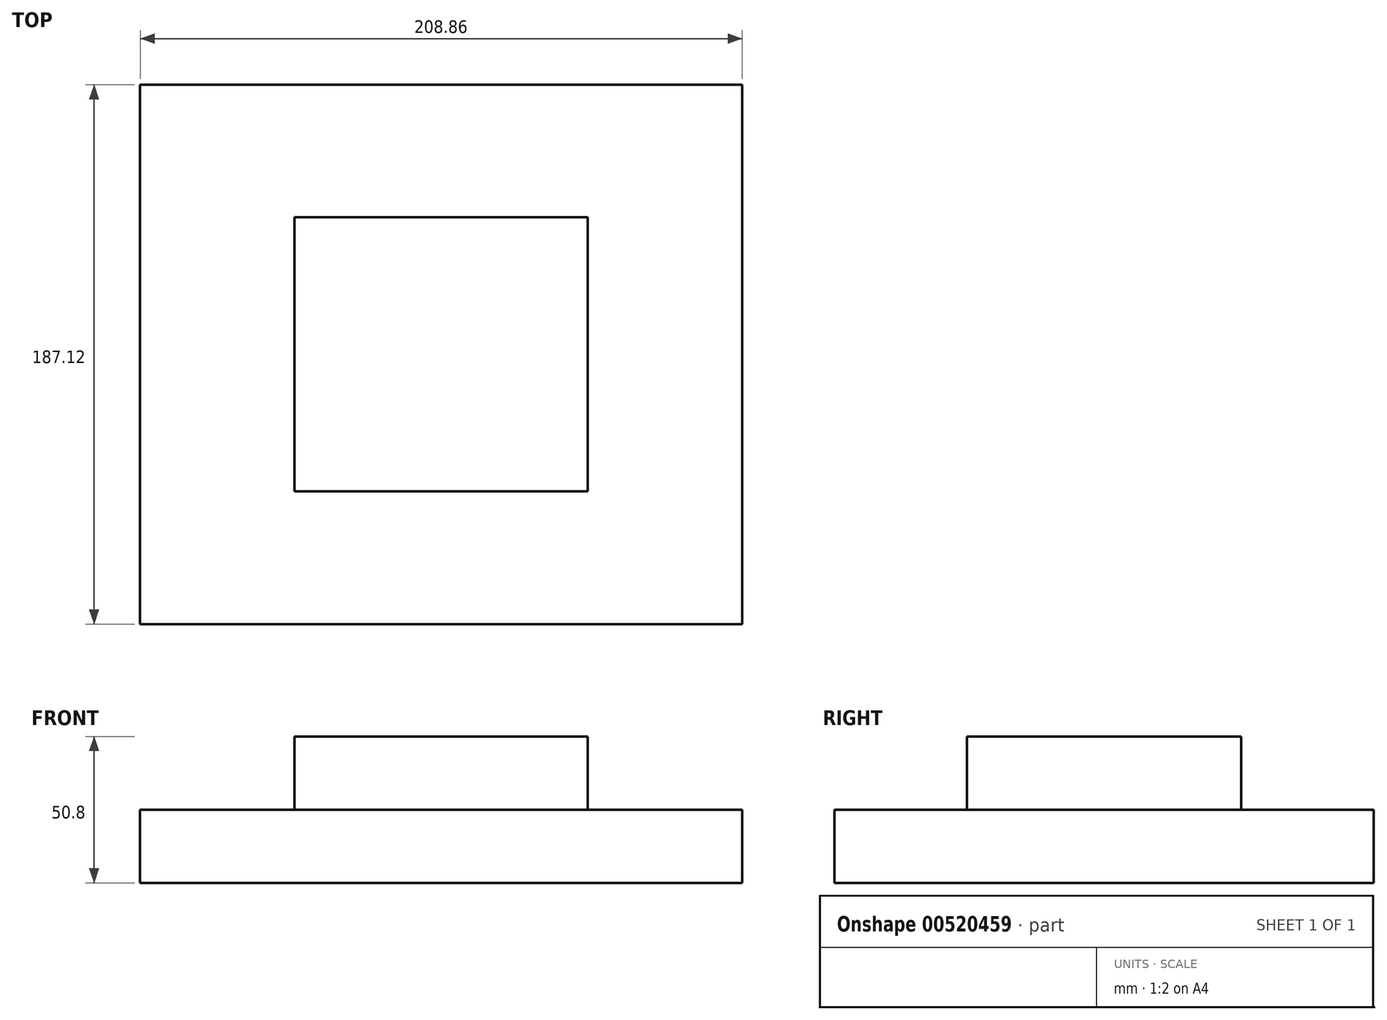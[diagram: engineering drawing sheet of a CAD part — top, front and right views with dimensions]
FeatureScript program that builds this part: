
annotation { "Feature Type Name" : "Feature", "Feature Type Description" : "" }
export const myFeature = defineFeature(function(context is Context, id is Id, definition is map)
    precondition{}
    {
        {
            var Q0;
            Q0=qCreatedBy(makeId("Top.planeOp"),FACE);
            var sketch = newSketch(context, id + "F0", { "sketchPlane" : qUnion([Q0])});
            skLineSegment(sketch, "E0.bottom", {"start": v(104.43, -93.56) * mm, "end": v(-104.43, -93.56) * mm});
            skLineSegment(sketch, "E0.top", {"start": v(104.43, 93.56) * mm, "end": v(-104.43, 93.56) * mm});
            skLineSegment(sketch, "E0.left", {"start": v(104.43, -93.56) * mm, "end": v(104.43, 93.56) * mm});
            skLineSegment(sketch, "E0.right", {"start": v(-104.43, -93.56) * mm, "end": v(-104.43, 93.56) * mm});
            skPoint(sketch, "E0.middle", {"position": v(0, 0) * mm});
            skLineSegment(sketch, "E1.bottom", {"start": v(45.8, -39.4) * mm, "end": v(-45.8, -39.4) * mm});
            skLineSegment(sketch, "E1.top", {"start": v(45.8, 39.4) * mm, "end": v(-45.8, 39.4) * mm});
            skLineSegment(sketch, "E1.left", {"start": v(45.8, -39.4) * mm, "end": v(45.8, 39.4) * mm});
            skLineSegment(sketch, "E1.right", {"start": v(-45.8, -39.4) * mm, "end": v(-45.8, 39.4) * mm});
            skSolve(sketch);
        }
        {
            var Q0;
            Q0=makeQuery(id+"F0.imprint","IMPRINT",FACE,{"disambiguationData":[TD([[makeQuery(id+"F0.imprint","IMPRINT",EDGE,{"derivedFrom":sQuery(id+"F0.wireOp",EDGE,"E0.bottom")}),-1.0]])]});
            var Q1;
            Q1=makeQuery(id+"F0.imprint","IMPRINT",FACE,{"disambiguationData":[TD([[makeQuery(id+"F0.imprint","IMPRINT",EDGE,{"derivedFrom":sQuery(id+"F0.wireOp",EDGE,"E1.bottom")}),-1.0]])]});
            extrude(context, id + "F1", {"entities" : qUnion([Q0, Q1]), "depth" : 25.4 * mm, "offsetDistance" : 25.4 * mm});
        }
        {
            var Q0;
            Q0=makeQuery(id+"F1.opExtrude","CAP_FACE",FACE,{"disambiguationData":[OSD([sQuery(id+"F0.wireOp",EDGE,"E0.bottom"),sQuery(id+"F0.wireOp",EDGE,"E0.top"),sQuery(id+"F0.wireOp",EDGE,"E0.left"),sQuery(id+"F0.wireOp",EDGE,"E0.right")])],"isStart":false});
            var sketch = newSketch(context, id + "F2", { "sketchPlane" : qUnion([Q0])});
            skLineSegment(sketch, "E2.bottom", {"start": v(-50.88, 47.55) * mm, "end": v(50.88, 47.55) * mm});
            skLineSegment(sketch, "E2.top", {"start": v(-50.88, -47.55) * mm, "end": v(50.88, -47.55) * mm});
            skLineSegment(sketch, "E2.left", {"start": v(-50.88, 47.55) * mm, "end": v(-50.88, -47.55) * mm});
            skLineSegment(sketch, "E2.right", {"start": v(50.88, 47.55) * mm, "end": v(50.88, -47.55) * mm});
            skPoint(sketch, "E2.middle", {"position": v(0, 0) * mm});
            skSolve(sketch);
        }
        {
            var Q0;
            Q0 = qSketchRegion(id + "F2", true);
            extrude(context, id + "F3", {"entities" : qUnion([Q0]), "operationType" : NewBodyOperationType.ADD, "depth" : 25.4 * mm, "offsetDistance" : 25.4 * mm});
        }
    });
